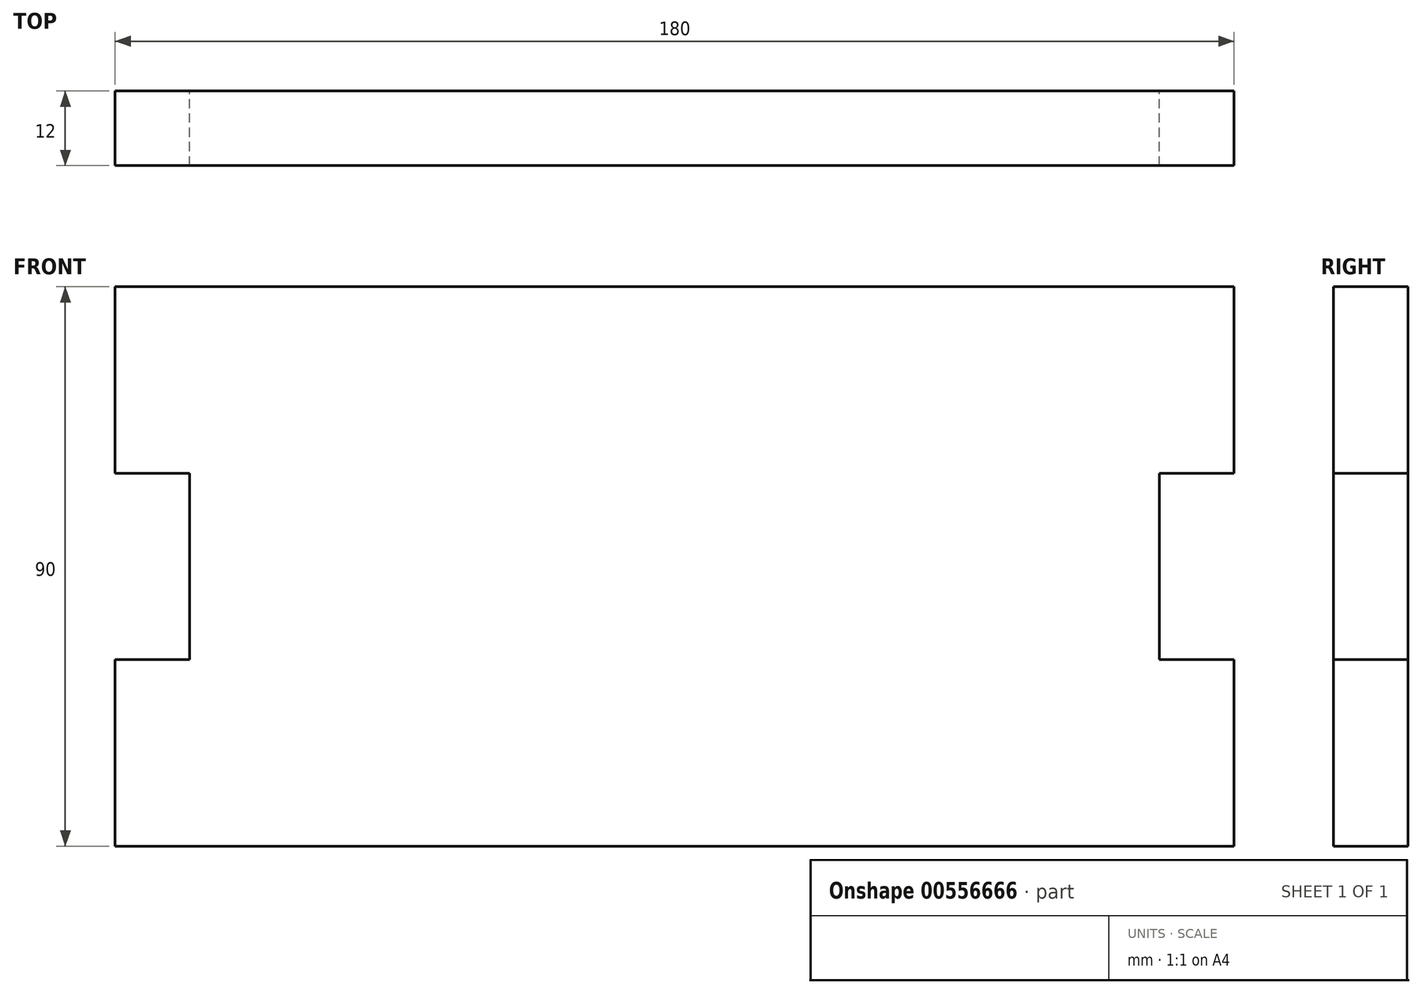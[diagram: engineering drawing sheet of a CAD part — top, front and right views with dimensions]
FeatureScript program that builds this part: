
annotation { "Feature Type Name" : "Feature", "Feature Type Description" : "" }
export const myFeature = defineFeature(function(context is Context, id is Id, definition is map)
    precondition{}
    {
        {
            var Q0;
            Q0=qCreatedBy(makeId("Front.planeOp"),FACE);
            var sketch = newSketch(context, id + "F0", { "sketchPlane" : qUnion([Q0])});
            skLineSegment(sketch, "E0", {"start": v(0, 0) * mm, "end": v(0, 30) * mm});
            skLineSegment(sketch, "E1", {"start": v(0, 30) * mm, "end": v(12, 30) * mm});
            skLineSegment(sketch, "E2", {"start": v(12, 30) * mm, "end": v(12, 60) * mm});
            skLineSegment(sketch, "E3", {"start": v(12, 60) * mm, "end": v(0, 60) * mm});
            skLineSegment(sketch, "E4", {"start": v(0, 60) * mm, "end": v(0, 90) * mm});
            skLineSegment(sketch, "E5", {"start": v(0, 90) * mm, "end": v(180, 90) * mm});
            skLineSegment(sketch, "E6", {"start": v(180, 90) * mm, "end": v(180, 60) * mm});
            skLineSegment(sketch, "E7", {"start": v(180, 60) * mm, "end": v(168, 60) * mm});
            skLineSegment(sketch, "E8", {"start": v(168, 60) * mm, "end": v(168, 30) * mm});
            skLineSegment(sketch, "E9", {"start": v(168, 30) * mm, "end": v(180, 30) * mm});
            skLineSegment(sketch, "E10", {"start": v(180, 30) * mm, "end": v(180, 0) * mm});
            skLineSegment(sketch, "E11", {"start": v(180, 0) * mm, "end": v(0, 0) * mm});
            skSolve(sketch);
        }
        {
            var Q0;
            Q0=makeQuery(id+"F0.imprint","IMPRINT",FACE,{"disambiguationData":[TD([[makeQuery(id+"F0.imprint","IMPRINT",EDGE,{"derivedFrom":sQuery(id+"F0.wireOp",EDGE,"E0")}),-1.0]])]});
            extrude(context, id + "F1", {"entities" : qUnion([Q0]), "depth" : 12 * mm, "offsetDistance" : 25 * mm});
        }
    });
